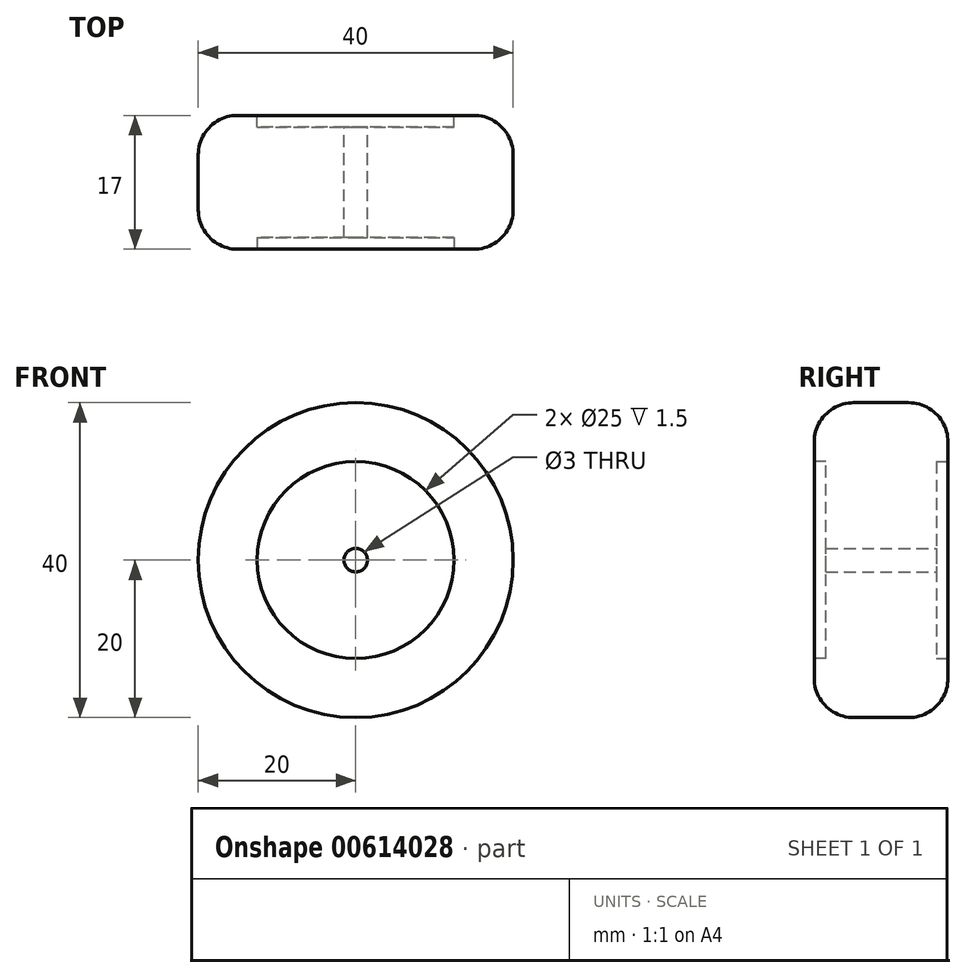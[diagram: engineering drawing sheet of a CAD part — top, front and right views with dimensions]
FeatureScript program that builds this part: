
annotation { "Feature Type Name" : "Feature", "Feature Type Description" : "" }
export const myFeature = defineFeature(function(context is Context, id is Id, definition is map)
    precondition{}
    {
        {
            var Q0;
            Q0=qCreatedBy(makeId("Front.planeOp"),FACE);
            var sketch = newSketch(context, id + "F0", { "sketchPlane" : qUnion([Q0])});
            skCircle(sketch, "E0", {"center": v(0, 0) * mm, "radius": 20 * mm});
            skCircle(sketch, "E1", {"center": v(0, 0) * mm, "radius": 1.5 * mm});
            skSolve(sketch);
        }
        {
            var Q0;
            Q0=makeQuery(id+"F0.imprint","IMPRINT",FACE,{"disambiguationData":[TD([[makeQuery(id+"F0.imprint","IMPRINT",EDGE,{"derivedFrom":sQuery(id+"F0.wireOp",EDGE,"E0")}),1.0]])]});
            extrude(context, id + "F1", {"entities" : qUnion([Q0]), "depth" : 17 * mm});
        }
        {
            var Q0;
            Q0=makeQuery(id+"F1.opExtrude","CAP_FACE",FACE,{"disambiguationData":[OSD([sQuery(id+"F0.wireOp",EDGE,"E0"),sQuery(id+"F0.wireOp",EDGE,"E1")])],"isStart":true});
            var sketch = newSketch(context, id + "F2", { "sketchPlane" : qUnion([Q0])});
            skCircle(sketch, "E2", {"center": v(0, 0) * mm, "radius": 12.5 * mm});
            skSolve(sketch);
        }
        {
            var Q0;
            Q0=qSketchRegion(id+"F2",true);
            extrude(context, id + "F3", {"entities" : qUnion([Q0]), "operationType" : NewBodyOperationType.REMOVE, "oppositeDirection" : true, "depth" : 1.5 * mm});
        }
        {
            var Q0;
            Q0=makeQuery(id+"F1.opExtrude","CAP_FACE",FACE,{"disambiguationData":[OSD([sQuery(id+"F0.wireOp",EDGE,"E0"),sQuery(id+"F0.wireOp",EDGE,"E1")])],"isStart":false});
            var sketch = newSketch(context, id + "F4", { "sketchPlane" : qUnion([Q0])});
            skCircle(sketch, "E3", {"center": v(0, 0) * mm, "radius": 12.5 * mm});
            skSolve(sketch);
        }
        {
            var Q0;
            Q0=makeQuery(id+"F4.imprint","IMPRINT",FACE,{"disambiguationData":[TD([[makeQuery(id+"F4.imprint","IMPRINT",EDGE,{"derivedFrom":sQuery(id+"F4.wireOp",EDGE,"E3")}),1.0]])]});
            extrude(context, id + "F5", {"entities" : qUnion([Q0]), "operationType" : NewBodyOperationType.REMOVE, "oppositeDirection" : true, "depth" : 1.5 * mm});
        }
        {
            var Q0;
            Q0=makeQuery(id+"F1.opExtrude","CAP_EDGE",EDGE,{"disambiguationData":[OSD([sQuery(id+"F0.wireOp",EDGE,"E0")])],"isStart":true});
            var Q1;
            Q1=makeQuery(id+"F1.opExtrude","CAP_EDGE",EDGE,{"disambiguationData":[OSD([sQuery(id+"F0.wireOp",EDGE,"E0")])],"isStart":false});
            fillet(context, id + "F6", {"entities" : qUnion([Q0, Q1]), "radius" : 5 * mm, "tangentPropagation" : true, "allowEdgeOverflow" : false});
        }
    });
